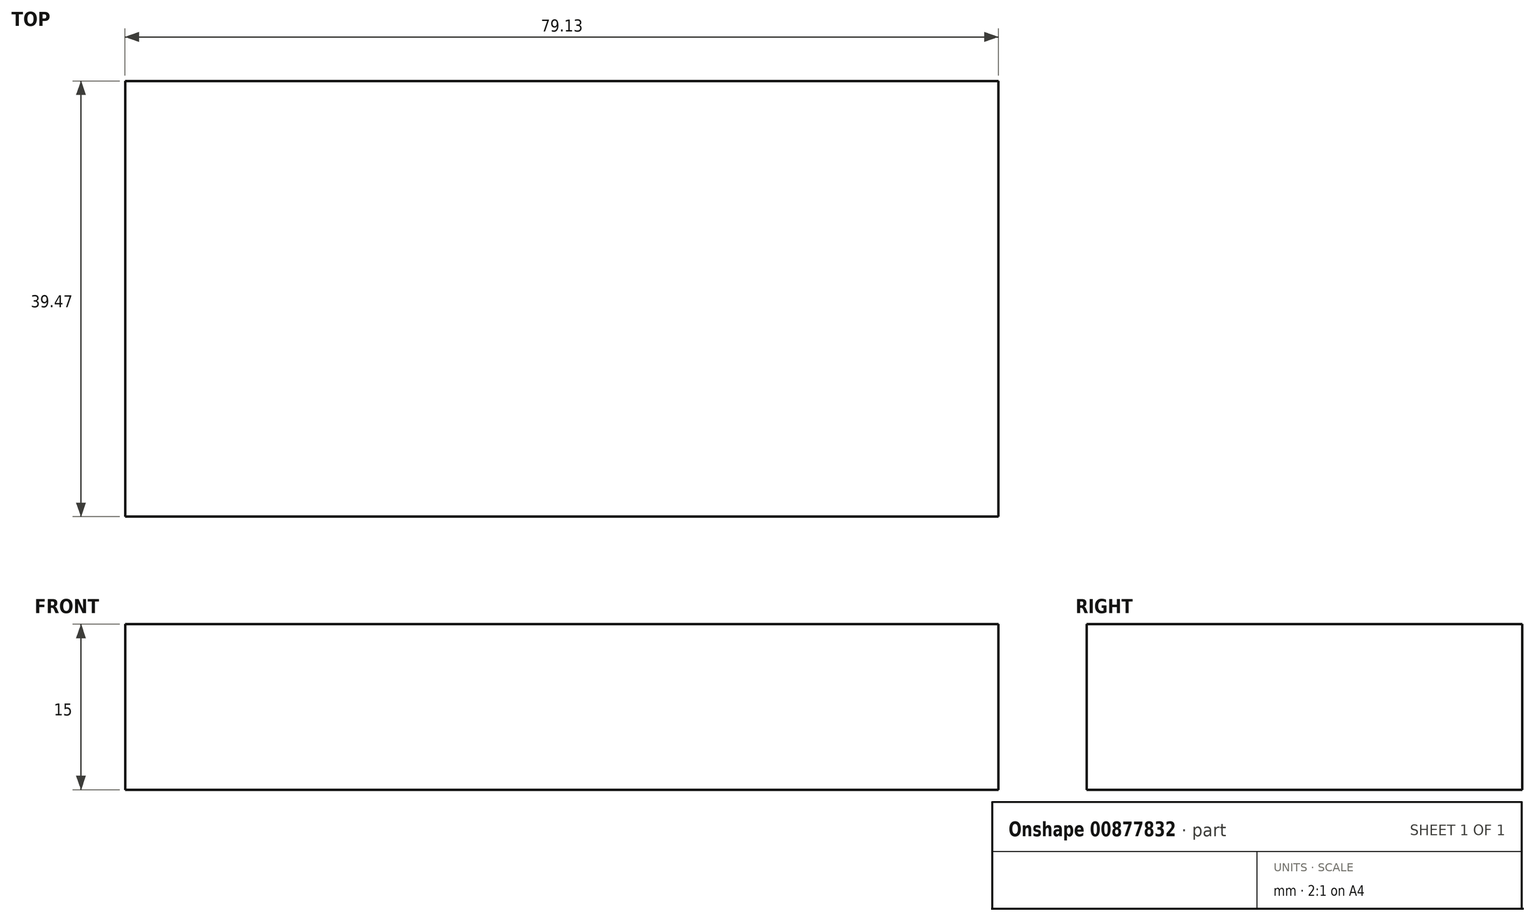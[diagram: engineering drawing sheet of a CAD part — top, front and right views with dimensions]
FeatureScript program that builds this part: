
annotation { "Feature Type Name" : "Feature", "Feature Type Description" : "" }
export const myFeature = defineFeature(function(context is Context, id is Id, definition is map)
    precondition{}
    {
        {
            var Q0;
            Q0=qCreatedBy(makeId("Top.planeOp"),FACE);
            var sketch = newSketch(context, id + "F0", { "sketchPlane" : qUnion([Q0])});
            skLineSegment(sketch, "E0.bottom", {"start": v(-29.79, 16.63) * mm, "end": v(49.34, 16.63) * mm});
            skLineSegment(sketch, "E0.top", {"start": v(-29.79, -22.84) * mm, "end": v(49.34, -22.84) * mm});
            skLineSegment(sketch, "E0.left", {"start": v(-29.79, 16.63) * mm, "end": v(-29.79, -22.84) * mm});
            skLineSegment(sketch, "E0.right", {"start": v(49.34, 16.63) * mm, "end": v(49.34, -22.84) * mm});
            skSolve(sketch);
        }
        {
            var Q0;
            Q0=makeQuery(id+"F0.imprint","IMPRINT",FACE,{"disambiguationData":[TD([[makeQuery(id+"F0.imprint","IMPRINT",EDGE,{"derivedFrom":sQuery(id+"F0.wireOp",EDGE,"E0.bottom")}),-1.0]])]});
            extrude(context, id + "F1", {"entities" : qUnion([Q0]), "depth" : 15 * mm, "offsetDistance" : 25 * mm});
        }
    });
